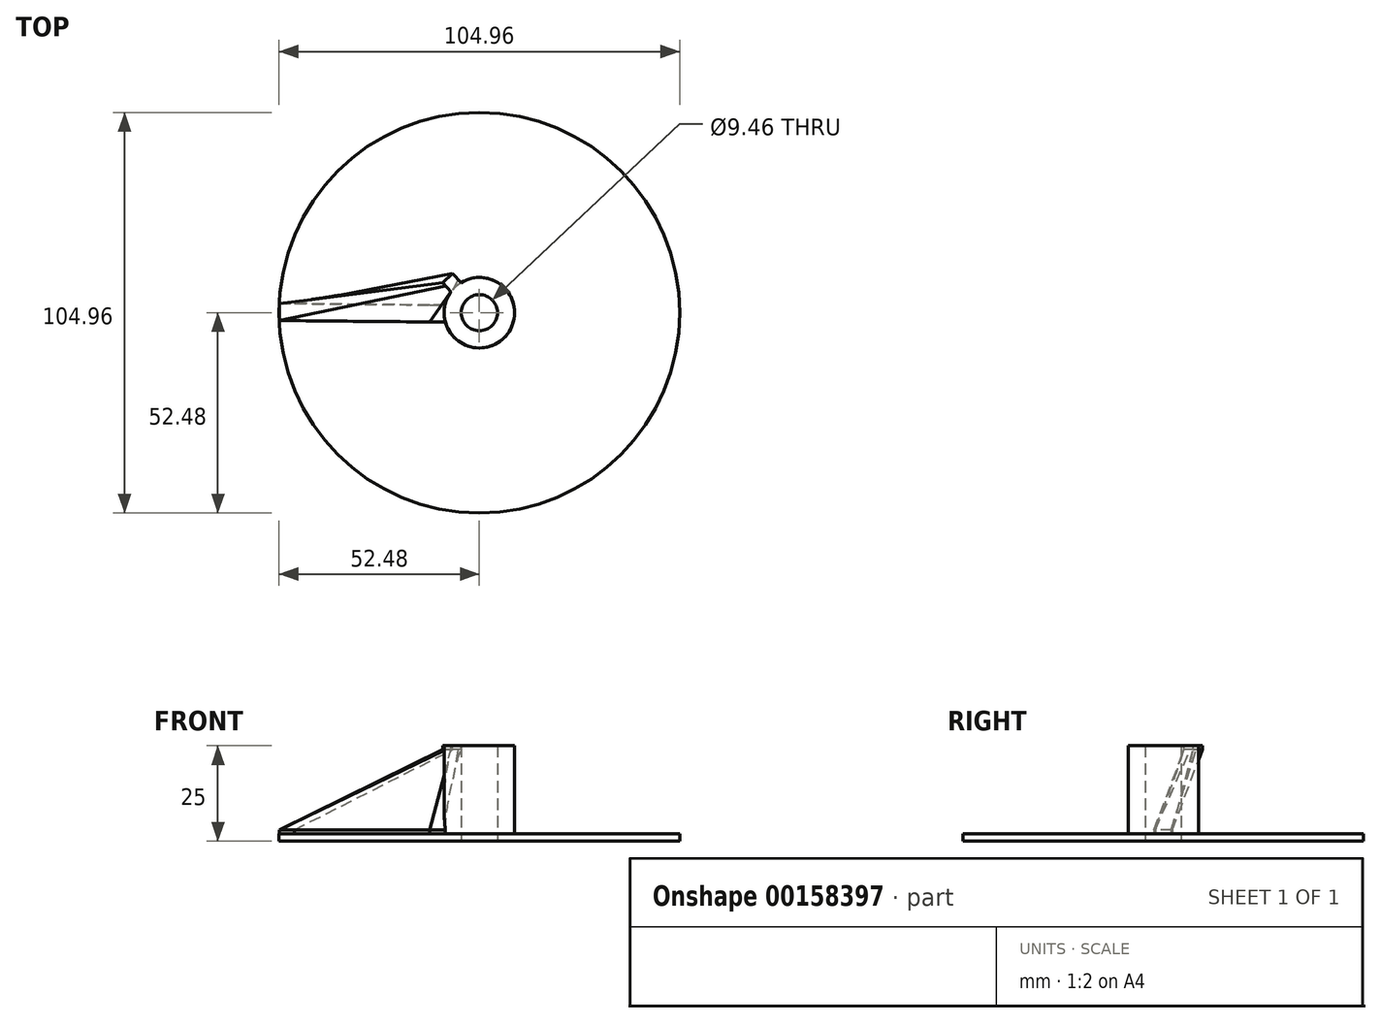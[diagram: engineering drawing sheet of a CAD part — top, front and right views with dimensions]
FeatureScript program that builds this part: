
annotation { "Feature Type Name" : "Feature", "Feature Type Description" : "" }
export const myFeature = defineFeature(function(context is Context, id is Id, definition is map)
    precondition{}
    {
        {
            var Q0;
            Q0=qCreatedBy(makeId("Top.planeOp"),FACE);
            var sketch = newSketch(context, id + "F0", { "sketchPlane" : qUnion([Q0])});
            skCircle(sketch, "E0", {"center": v(0, 0) * mm, "radius": 4.73 * mm});
            skCircle(sketch, "E1.0", {"center": v(0, 0) * mm, "radius": 9.23 * mm});
            skCircle(sketch, "E2.0", {"center": v(0, 0) * mm, "radius": 52.48 * mm});
            skSolve(sketch);
        }
        {
            var Q0;
            Q0=makeQuery(id+"F0.imprint","IMPRINT",FACE,{"disambiguationData":[TD([[makeQuery(id+"F0.imprint","IMPRINT",EDGE,{"derivedFrom":sQuery(id+"F0.wireOp",EDGE,"E0")}),-1.0]])]});
            extrude(context, id + "F1", {"entities" : qUnion([Q0]), "depth" : 25 * mm});
        }
        {
            var Q0;
            Q0=makeQuery(id+"F0.imprint","IMPRINT",FACE,{"disambiguationData":[TD([[makeQuery(id+"F0.imprint","IMPRINT",EDGE,{"derivedFrom":sQuery(id+"F0.wireOp",EDGE,"E1.0")}),-1.0]])]});
            extrude(context, id + "F2", {"entities" : qUnion([Q0]), "operationType" : NewBodyOperationType.ADD, "depth" : 2 * mm});
        }
        {
            var Q0;
            Q0=makeQuery(id+"F2.opExtrude","CAP_FACE",FACE,{"disambiguationData":[OSD([sQuery(id+"F0.wireOp",EDGE,"E1.0"),sQuery(id+"F0.wireOp",EDGE,"E2.0")])],"isStart":false});
            var sketch = newSketch(context, id + "F3", { "sketchPlane" : qUnion([Q0])});
            skLineSegment(sketch, "E3.bottom", {"start": v(-52.43, 2.38) * mm, "end": v(-48.43, 2.38) * mm});
            skLineSegment(sketch, "E3.top", {"start": v(-52.43, -2.08) * mm, "end": v(-48.43, -2.08) * mm});
            skLineSegment(sketch, "E3.left", {"start": v(-52.43, 2.38) * mm, "end": v(-52.43, -2.08) * mm});
            skLineSegment(sketch, "E3.right", {"start": v(-48.43, 2.38) * mm, "end": v(-48.43, -2.08) * mm});
            skLineSegment(sketch, "E4.bottom", {"start": v(-9, 2.03) * mm, "end": v(-13, 2.03) * mm});
            skLineSegment(sketch, "E4.top", {"start": v(-9, -2.43) * mm, "end": v(-13, -2.43) * mm});
            skLineSegment(sketch, "E4.left", {"start": v(-9, 2.03) * mm, "end": v(-9, -2.43) * mm});
            skLineSegment(sketch, "E4.right", {"start": v(-13, 2.03) * mm, "end": v(-13, -2.43) * mm});
            skLineSegment(sketch, "E5", {"start": v(-13, -0.2) * mm, "end": v(-9.23, -0.2) * mm, "construction": true});
            skSolve(sketch);
        }
        {
            var Q0;
            Q0=makeQuery(id+"F1.opExtrude","CAP_FACE",FACE,{"disambiguationData":[OSD([sQuery(id+"F0.wireOp",EDGE,"E0"),sQuery(id+"F0.wireOp",EDGE,"E1.0")])],"isStart":false});
            var sketch = newSketch(context, id + "F4", { "sketchPlane" : qUnion([Q0])});
            skLineSegment(sketch, "E6", {"start": v(-4.81, 7.88) * mm, "end": v(-7, 10.25) * mm});
            skLineSegment(sketch, "E7", {"start": v(-7, 10.25) * mm, "end": v(-9.63, 7.83) * mm});
            skLineSegment(sketch, "E8", {"start": v(-9.63, 7.83) * mm, "end": v(-7.45, 5.46) * mm});
            skSolve(sketch);
        }
        {
            var Q0;
            {var subQ0=sQuery(id+"F4.wireOp",EDGE,"E6");Q0=makeQuery(id+"F4.imprint","IMPRINT",FACE,{"disambiguationData":[TD([[makeQuery(id+"F4.imprint","IMPRINT",EDGE,{"derivedFrom":subQ0}),1.0]])]});}
            extrude(context, id + "F5", {"entities" : qUnion([Q0]), "operationType" : NewBodyOperationType.ADD, "oppositeDirection" : true, "depth" : 1 * mm});
        }
        {
            var Q0;
            {var subQ4=sQuery(id+"F3.wireOp",EDGE,"E4.bottom");Q0=makeQuery(id+"F3.imprint","IMPRINT",FACE,{"disambiguationData":[TD([[makeQuery(id+"F3.imprint","IMPRINT",EDGE,{"derivedFrom":subQ4}),1.0]])]});}
            var Q1;
            Q1=makeQuery(id+"F3.imprint","IMPRINT",FACE,{"disambiguationData":[TD([[makeQuery(id+"F3.imprint","IMPRINT",EDGE,{"derivedFrom":sQuery(id+"F3.wireOp",EDGE,"E3.bottom")}),-1.0]])]});
            extrude(context, id + "F6", {"entities" : qUnion([Q0, Q1]), "operationType" : NewBodyOperationType.ADD, "depth" : 1 * mm});
        }
        {
            var Q1;
            Q1=makeQuery(id+"F6.opExtrude","SWEPT_FACE",FACE,{"disambiguationData":[OSD([sQuery(id+"F3.wireOp",EDGE,"E4.right")])]});
            var Q2;
            Q2=makeQuery(id+"F6.opExtrude","SWEPT_FACE",FACE,{"disambiguationData":[OSD([sQuery(id+"F3.wireOp",EDGE,"E3.right")])]});
            loft(context, id + "F7", {"operationType" : NewBodyOperationType.ADD, "sheetProfilesArray" : [{ "sheetProfileEntities" : qUnion([Q1]) }, { "sheetProfileEntities" : qUnion([Q2]) }]});
        }
        {
            var Q1;
            {var subQ0=sQuery(id+"F3.wireOp",EDGE,"E4.right");var subQ1=sQuery(id+"F3.wireOp",EDGE,"E3.right");var subQ2=sQuery(id+"F3.wireOp",EDGE,"E4.top");var subQ3=sQuery(id+"F3.wireOp",EDGE,"E4.bottom");var subQ4=sQuery(id+"F3.wireOp",EDGE,"E3.top");var subQ5=sQuery(id+"F3.wireOp",EDGE,"E3.bottom");Q1=makeQuery(id+"F7.boolean.opBoolean","MERGE",FACE,{"derivedFrom":[makeQuery(id+"F6.opExtrude","CAP_FACE",FACE,{"disambiguationData":[OSD([subQ5,subQ4,sQuery(id+"F3.wireOp",EDGE,"E3.left"),subQ1])],"isStart":false}),makeQuery(id+"F6.opExtrude","CAP_FACE",FACE,{"disambiguationData":[OSD([sQuery(id+"F0.wireOp",EDGE,"E1.0"),subQ3,subQ2,sQuery(id+"F3.wireOp",EDGE,"E4.left"),subQ0])],"isStart":false}),makeQuery(id+"F7.opLoft","SWEPT_FACE",FACE,{"disambiguationData":[OSD([subQ5,subQ4,subQ1,subQ3,subQ2,subQ0]),TDD([makeQuery(id+"F6.opExtrude","CAP_VERTEX",VERTEX,{"disambiguationData":[OSD([subQ5,subQ1])],"isStart":false}),makeQuery(id+"F6.opExtrude","CAP_VERTEX",VERTEX,{"disambiguationData":[OSD([subQ4,subQ1])],"isStart":false}),makeQuery(id+"F6.opExtrude","CAP_VERTEX",VERTEX,{"disambiguationData":[OSD([subQ3,subQ0])],"isStart":false}),makeQuery(id+"F6.opExtrude","CAP_VERTEX",VERTEX,{"disambiguationData":[OSD([subQ2,subQ0])],"isStart":false}),makeQuery(id+"F6.opExtrude","CAP_EDGE",EDGE,{"disambiguationData":[OSD([subQ1])],"isStart":false}),makeQuery(id+"F6.opExtrude","CAP_EDGE",EDGE,{"disambiguationData":[OSD([subQ0])],"isStart":false})])]})]});}
            var Q2;
            Q2=makeQuery(id+"F5.opExtrude","CAP_FACE",FACE,{"disambiguationData":[OSD([sQuery(id+"F0.wireOp",EDGE,"E1.0"),sQuery(id+"F4.wireOp",EDGE,"E6"),sQuery(id+"F4.wireOp",EDGE,"E7"),sQuery(id+"F4.wireOp",EDGE,"E8")])],"isStart":false});
            loft(context, id + "F8", {"operationType" : NewBodyOperationType.ADD, "sheetProfilesArray" : [{ "sheetProfileEntities" : qUnion([Q1]) }, { "sheetProfileEntities" : qUnion([Q2]) }]});
        }
    });
